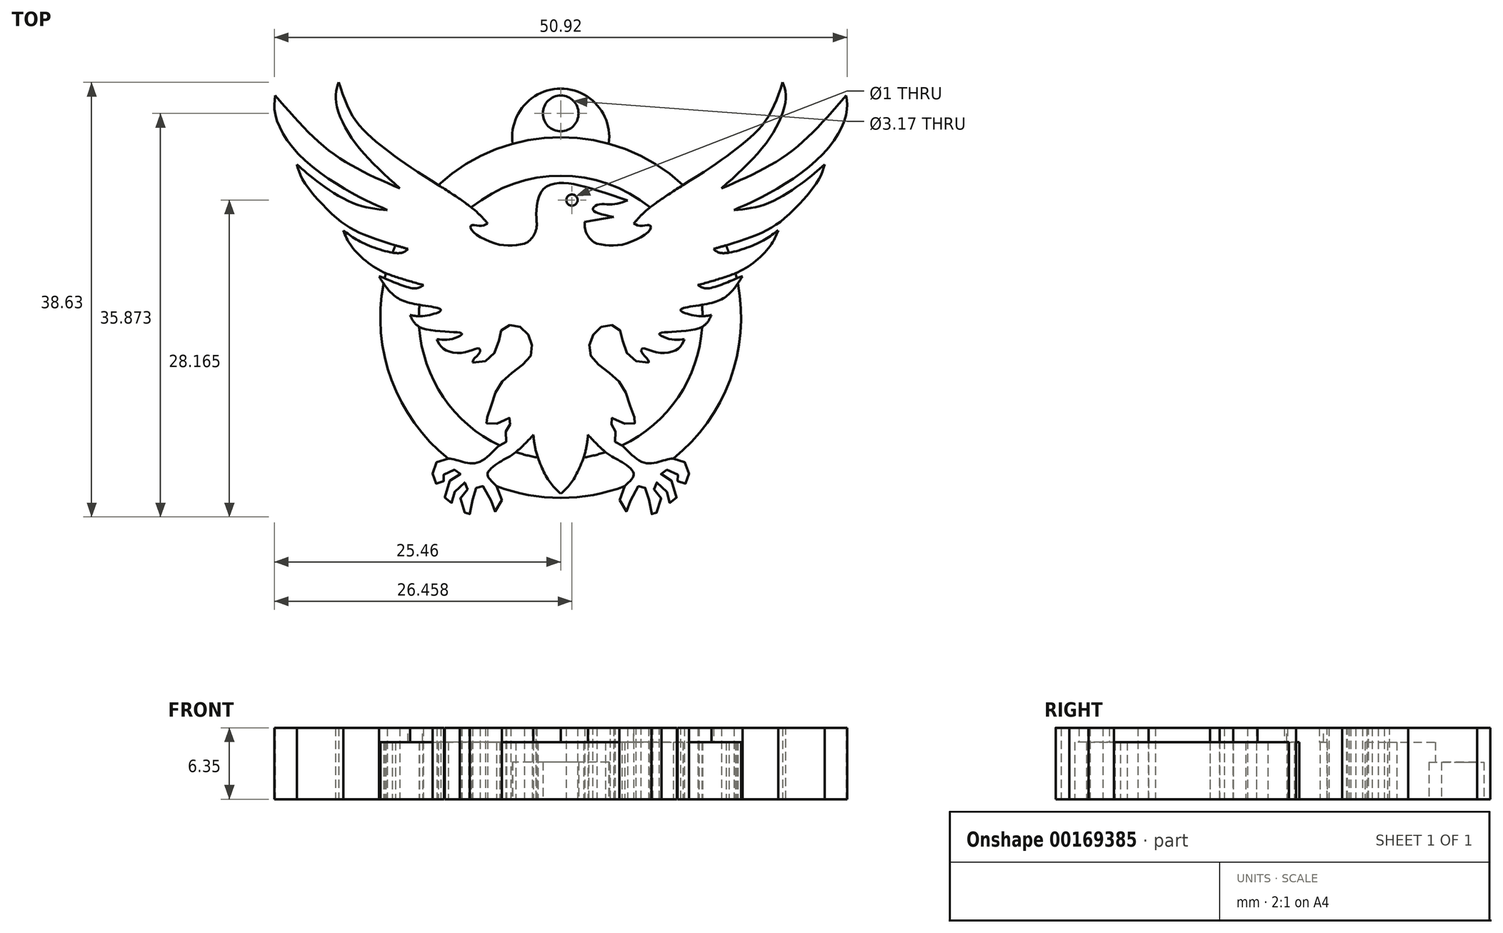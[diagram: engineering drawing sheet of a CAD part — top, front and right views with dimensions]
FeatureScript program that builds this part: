
annotation { "Feature Type Name" : "Feature", "Feature Type Description" : "" }
export const myFeature = defineFeature(function(context is Context, id is Id, definition is map)
    precondition{}
    {
        {
            var Q0;
            Q0=qCreatedBy(makeId("Top.planeOp"),FACE);
            var sketch = newSketch(context, id + "F0", { "sketchPlane" : qUnion([Q0])});
            skArc(sketch, "E0", {"start": v(-3.37, -10.71) * mm, "mid": v(-3.14, -11.87) * mm, "end": v(-2.29, -12.67) * mm});
            skFitSpline(sketch, "E1", {"points": [v(-2.29, -12.67) * mm, v(0.23, -12.67) * mm, v(2.47, -11.32) * mm, v(2.37, -11.01) * mm, v(1.64, -11.08) * mm, v(0.98, -10.87) * mm], "startDerivative": vector(8.17, -1.32) * mm, "endDerivative": vector(-4, 2.15) * mm});
            skFitSpline(sketch, "E2", {"points": [v(0.98, -10.87) * mm, v(2.44, -9.44) * mm, v(7.37, -6.17) * mm, v(10.62, -3.82) * mm, v(12.83, -1.57) * mm, v(14.23, 1.68) * mm], "startDerivative": vector(7.54, 8.8) * mm, "endDerivative": vector(5.9, 17.53) * mm});
            skFitSpline(sketch, "E3", {"points": [v(14.23, 1.68) * mm, v(14.5, 0.33) * mm, v(13.2, -3.1) * mm, v(8.8, -7.74) * mm], "startDerivative": vector(2.08, -5.75) * mm, "endDerivative": vector(-11.1, -10.06) * mm});
            skFitSpline(sketch, "E4", {"points": [v(8.8, -7.74) * mm, v(14.77, -4.61) * mm, v(19.87, 0.5) * mm], "startDerivative": vector(12.68, 5.47) * mm, "endDerivative": vector(9.48, 11) * mm});
            skFitSpline(sketch, "E5", {"points": [v(19.87, 0.5) * mm, v(19.87, -1.18) * mm, v(17.7, -4.8) * mm, v(12.52, -8.44) * mm, v(9.9, -9.66) * mm], "startDerivative": vector(1.23, -9.08) * mm, "endDerivative": vector(-10.45, -4.42) * mm});
            skFitSpline(sketch, "E6", {"points": [v(9.9, -9.66) * mm, v(12.85, -9.1) * mm, v(16.4, -6.93) * mm, v(17.95, -5.6) * mm], "startDerivative": vector(8.57, 0.68) * mm, "endDerivative": vector(4.89, 4.45) * mm});
            skFitSpline(sketch, "E7", {"points": [v(17.95, -5.6) * mm, v(17.36, -7.07) * mm, v(14.57, -10.25) * mm, v(12.16, -11.78) * mm, v(8.07, -13.13) * mm], "startDerivative": vector(-1.97, -7.45) * mm, "endDerivative": vector(-15.16, -4.48) * mm});
            skFitSpline(sketch, "E8", {"points": [v(8.07, -13.13) * mm, v(8.8, -13.5) * mm, v(11.88, -12.67) * mm, v(13.82, -11.49) * mm], "startDerivative": vector(2.56, -2.28) * mm, "endDerivative": vector(4.6, 3.34) * mm});
            skFitSpline(sketch, "E9", {"points": [v(13.82, -11.49) * mm, v(13.1, -12.89) * mm, v(11, -14.78) * mm, v(8.8, -15.73) * mm, v(6.7, -16.34) * mm], "startDerivative": vector(-2.57, -6.45) * mm, "endDerivative": vector(-8.46, -2.36) * mm});
            skFitSpline(sketch, "E10", {"points": [v(6.7, -16.34) * mm, v(7.58, -16.63) * mm, v(10.33, -15.66) * mm, v(10.64, -15.57) * mm], "startDerivative": vector(2.24, -1.67) * mm, "endDerivative": vector(1.2, 0.2) * mm});
            skFitSpline(sketch, "E11", {"points": [v(10.64, -15.57) * mm, v(9.7, -16.9) * mm, v(8.07, -17.88) * mm, v(5.25, -18.44) * mm, v(5.17, -18.62) * mm, v(6.7, -19.09) * mm, v(7.89, -19) * mm], "startDerivative": vector(-4.95, -7.81) * mm, "endDerivative": vector(6.73, 1.3) * mm});
            skFitSpline(sketch, "E12", {"points": [v(7.89, -19) * mm, v(6.86, -20.15) * mm, v(3.5, -20.57) * mm, v(3.27, -20.71) * mm, v(4.27, -21.16) * mm, v(5.5, -21.16) * mm], "startDerivative": vector(-2.87, -6.23) * mm, "endDerivative": vector(5.96, 0.75) * mm});
            skFitSpline(sketch, "E13", {"points": [v(5.5, -21.16) * mm, v(4.87, -22.04) * mm, v(3.02, -22.32) * mm, v(1.8, -21.98) * mm, v(1.66, -22.24) * mm, v(2.22, -22.94) * mm, v(2.32, -23.25) * mm], "startDerivative": vector(-2.34, -5.3) * mm, "endDerivative": vector(0.24, -2.7) * mm});
            skFitSpline(sketch, "E14", {"points": [v(2.32, -23.25) * mm, v(0.8, -22.88) * mm, v(0, -21.38) * mm, v(-0.27, -20.31) * mm, v(-1.2, -19.9) * mm, v(-2.29, -20.33) * mm, v(-2.9, -21.44) * mm, v(-2.86, -22.58) * mm, v(-1.78, -23.69) * mm, v(-0.41, -24.83) * mm, v(0.45, -26.34) * mm, v(0.98, -28) * mm, v(1.18, -28.53) * mm, v(0.45, -28.7) * mm, v(-0.45, -28.43) * mm, v(-0.77, -28.1) * mm, v(-1.01, -28.23) * mm, v(-1.01, -28.7) * mm, v(-0.65, -29.23) * mm, v(-0.67, -30.28) * mm, v(-0.21, -30.52) * mm, v(1.7, -32.07) * mm, v(3.59, -31.95) * mm, v(4.81, -31.78) * mm, v(5.72, -32.33) * mm, v(5.86, -33.43) * mm, v(5.5, -34.01) * mm, v(4.87, -33.83) * mm, v(5.15, -33.4) * mm, v(4.35, -33.01) * mm, v(3.75, -32.75) * mm, v(3.4, -33.11) * mm, v(4.25, -33.65) * mm, v(4.71, -35.5) * mm, v(4.2, -35.72) * mm, v(4.03, -34.98) * mm, v(3.06, -33.9) * mm, v(2.68, -34.28) * mm, v(3.04, -34.74) * mm, v(3.43, -35.82) * mm, v(2.6, -36.95) * mm, v(2.6, -36.24) * mm, v(2.04, -34.7) * mm, v(1.94, -34.2) * mm, v(1.38, -34.24) * mm, v(0.51, -36.1) * mm, v(0.31, -36.47) * mm, v(-0.3, -35.22) * mm, v(0.55, -33.85) * mm, v(0.98, -33.1) * mm, v(0, -32.13) * mm, v(-1.38, -31.3) * mm, v(-3.08, -29.65) * mm], "startDerivative": vector(-71.1, 3.05) * mm, "endDerivative": vector(-59.57, 64.05) * mm});
            skFitSpline(sketch, "E15", {"points": [v(-3.08, -29.65) * mm, v(-3.34, -31.24) * mm, v(-4.47, -33.75) * mm, v(-5.51, -34.9) * mm], "startDerivative": vector(-0.44, -4.8) * mm, "endDerivative": vector(-3.51, -3.2) * mm});
            skArc(sketch, "E16.MirrorCS", {"start": v(-7.65, -10.71) * mm, "mid": v(-7.88, -11.87) * mm, "end": v(-8.73, -12.67) * mm});
            skFitSpline(sketch, "E17.MirrorCS", {"points": [v(-8.73, -12.67) * mm, v(-11.25, -12.67) * mm, v(-13.5, -11.32) * mm, v(-13.4, -11.01) * mm, v(-12.66, -11.08) * mm, v(-12, -10.87) * mm], "startDerivative": vector(-8.17, -1.32) * mm, "endDerivative": vector(4, 2.15) * mm});
            skFitSpline(sketch, "E18.MirrorCS", {"points": [v(-12, -10.87) * mm, v(-13.46, -9.44) * mm, v(-18.4, -6.17) * mm, v(-21.64, -3.82) * mm, v(-23.85, -1.57) * mm, v(-25.25, 1.68) * mm], "startDerivative": vector(-7.54, 8.8) * mm, "endDerivative": vector(-5.9, 17.53) * mm});
            skFitSpline(sketch, "E19.MirrorCS", {"points": [v(-25.25, 1.68) * mm, v(-25.52, 0.33) * mm, v(-24.21, -3.1) * mm, v(-19.82, -7.74) * mm], "startDerivative": vector(-2.08, -5.75) * mm, "endDerivative": vector(11.1, -10.06) * mm});
            skFitSpline(sketch, "E20.MirrorCS", {"points": [v(-19.82, -7.74) * mm, v(-25.8, -4.61) * mm, v(-30.89, 0.5) * mm], "startDerivative": vector(-12.68, 5.47) * mm, "endDerivative": vector(-9.48, 11) * mm});
            skFitSpline(sketch, "E21.MirrorCS", {"points": [v(-30.89, 0.5) * mm, v(-30.89, -1.18) * mm, v(-28.72, -4.8) * mm, v(-23.54, -8.44) * mm, v(-20.92, -9.66) * mm], "startDerivative": vector(-1.23, -9.08) * mm, "endDerivative": vector(10.45, -4.42) * mm});
            skFitSpline(sketch, "E22.MirrorCS", {"points": [v(-20.92, -9.66) * mm, v(-23.87, -9.1) * mm, v(-27.42, -6.93) * mm, v(-28.97, -5.6) * mm], "startDerivative": vector(-8.57, 0.68) * mm, "endDerivative": vector(-4.89, 4.45) * mm});
            skFitSpline(sketch, "E23.MirrorCS", {"points": [v(-28.97, -5.6) * mm, v(-28.38, -7.07) * mm, v(-25.59, -10.25) * mm, v(-23.18, -11.78) * mm, v(-19.1, -13.13) * mm], "startDerivative": vector(1.97, -7.45) * mm, "endDerivative": vector(15.16, -4.48) * mm});
            skFitSpline(sketch, "E24.MirrorCS", {"points": [v(-19.1, -13.13) * mm, v(-19.82, -13.5) * mm, v(-22.9, -12.67) * mm, v(-24.84, -11.49) * mm], "startDerivative": vector(-2.56, -2.28) * mm, "endDerivative": vector(-4.6, 3.34) * mm});
            skFitSpline(sketch, "E25.MirrorCS", {"points": [v(-24.84, -11.49) * mm, v(-24.12, -12.89) * mm, v(-22.03, -14.78) * mm, v(-19.82, -15.73) * mm, v(-17.72, -16.34) * mm], "startDerivative": vector(2.57, -6.45) * mm, "endDerivative": vector(8.46, -2.36) * mm});
            skFitSpline(sketch, "E26.MirrorCS", {"points": [v(-17.72, -16.34) * mm, v(-18.6, -16.63) * mm, v(-21.35, -15.66) * mm, v(-21.66, -15.57) * mm], "startDerivative": vector(-2.24, -1.67) * mm, "endDerivative": vector(-1.2, 0.2) * mm});
            skFitSpline(sketch, "E27.MirrorCS", {"points": [v(-21.66, -15.57) * mm, v(-20.72, -16.9) * mm, v(-19.1, -17.88) * mm, v(-16.27, -18.44) * mm, v(-16.2, -18.62) * mm, v(-17.72, -19.09) * mm, v(-18.9, -19) * mm], "startDerivative": vector(4.95, -7.81) * mm, "endDerivative": vector(-6.73, 1.3) * mm});
            skFitSpline(sketch, "E28.MirrorCS", {"points": [v(-18.9, -19) * mm, v(-17.88, -20.15) * mm, v(-14.53, -20.57) * mm, v(-14.29, -20.71) * mm, v(-15.3, -21.16) * mm, v(-16.52, -21.16) * mm], "startDerivative": vector(2.87, -6.23) * mm, "endDerivative": vector(-5.96, 0.75) * mm});
            skFitSpline(sketch, "E29.MirrorCS", {"points": [v(-16.52, -21.16) * mm, v(-15.9, -22.04) * mm, v(-14.04, -22.32) * mm, v(-12.82, -21.98) * mm, v(-12.68, -22.24) * mm, v(-13.24, -22.94) * mm, v(-13.34, -23.25) * mm], "startDerivative": vector(2.34, -5.3) * mm, "endDerivative": vector(-0.24, -2.7) * mm});
            skFitSpline(sketch, "E30.MirrorCS", {"points": [v(-13.34, -23.25) * mm, v(-11.81, -22.88) * mm, v(-11.02, -21.38) * mm, v(-10.75, -20.31) * mm, v(-9.83, -19.9) * mm, v(-8.73, -20.33) * mm, v(-8.12, -21.44) * mm, v(-8.16, -22.58) * mm, v(-9.24, -23.69) * mm, v(-10.6, -24.83) * mm, v(-11.47, -26.34) * mm, v(-12, -28) * mm, v(-12.2, -28.53) * mm, v(-11.47, -28.7) * mm, v(-10.57, -28.43) * mm, v(-10.25, -28.1) * mm, v(-10, -28.23) * mm, v(-10, -28.7) * mm, v(-10.37, -29.23) * mm, v(-10.35, -30.28) * mm, v(-10.8, -30.52) * mm, v(-12.72, -32.07) * mm, v(-14.6, -31.95) * mm, v(-15.83, -31.78) * mm, v(-16.74, -32.33) * mm, v(-16.88, -33.43) * mm, v(-16.52, -34.01) * mm, v(-15.9, -33.83) * mm, v(-16.17, -33.4) * mm, v(-15.37, -33.01) * mm, v(-14.77, -32.75) * mm, v(-14.43, -33.11) * mm, v(-15.27, -33.65) * mm, v(-15.73, -35.5) * mm, v(-15.23, -35.72) * mm, v(-15.05, -34.98) * mm, v(-14.08, -33.9) * mm, v(-13.7, -34.28) * mm, v(-14.06, -34.74) * mm, v(-14.45, -35.82) * mm, v(-13.62, -36.95) * mm, v(-13.62, -36.24) * mm, v(-13.06, -34.7) * mm, v(-12.96, -34.2) * mm, v(-12.4, -34.24) * mm, v(-11.53, -36.1) * mm, v(-11.33, -36.47) * mm, v(-10.73, -35.22) * mm, v(-11.57, -33.85) * mm, v(-12, -33.1) * mm, v(-11.02, -32.13) * mm, v(-9.64, -31.3) * mm, v(-7.94, -29.65) * mm], "startDerivative": vector(71.1, 3.05) * mm, "endDerivative": vector(59.57, 64.05) * mm});
            skFitSpline(sketch, "E31.MirrorCS", {"points": [v(-7.94, -29.65) * mm, v(-7.68, -31.24) * mm, v(-6.55, -33.75) * mm, v(-5.51, -34.9) * mm], "startDerivative": vector(0.44, -4.8) * mm, "endDerivative": vector(3.51, -3.2) * mm});
            skArc(sketch, "E32", {"start": v(-11.21, -34.22) * mm, "mid": v(-5.51, -35.27) * mm, "end": v(0.2, -34.22) * mm});
            skArc(sketch, "E33", {"start": v(-9.5, -31.2) * mm, "mid": v(-8.53, -31.47) * mm, "end": v(-7.54, -31.68) * mm});
            skFitSpline(sketch, "E34", {"points": [v(-7.65, -10.71) * mm, v(-7.65, -9.41) * mm, v(-7.12, -7.88) * mm, v(-5.8, -7.27) * mm, v(-3.69, -7.51) * mm, v(0.44, -8.8) * mm], "startDerivative": vector(-0.46, 7.77) * mm, "endDerivative": vector(15.27, -5.17) * mm});
            skFitSpline(sketch, "E35", {"points": [v(0.44, -8.8) * mm, v(-0.98, -9.16) * mm, v(-2.24, -9.2) * mm, v(-2.65, -9.64) * mm, v(-0.81, -10.28) * mm], "startDerivative": vector(-5.23, -1.83) * mm, "endDerivative": vector(8.52, -1.74) * mm});
            skLineSegment(sketch, "E36", {"start": v(-3.37, -10.71) * mm, "end": v(-0.81, -10.28) * mm});
            skCircle(sketch, "E37", {"center": v(-4.51, -8.78) * mm, "radius": 0.5 * mm});
            skArc(sketch, "E38", {"start": v(-1.23, -3.77) * mm, "mid": v(-5.51, 1.12) * mm, "end": v(-9.79, -3.77) * mm});
            skCircle(sketch, "E39", {"center": v(-5.51, -1.08) * mm, "radius": 1.59 * mm});
            skArc(sketch, "E40.trimOffspring", {"start": v(-0.07, -30.6) * mm, "mid": v(4.93, -26.3) * mm, "end": v(7.07, -20.05) * mm});
            skArc(sketch, "E41.trimOffspring", {"start": v(-3.48, -31.68) * mm, "mid": v(-2.49, -31.47) * mm, "end": v(-1.52, -31.2) * mm});
            skArc(sketch, "E42.trimOffspring", {"start": v(4.49, -31.77) * mm, "mid": v(9.53, -24.78) * mm, "end": v(10.24, -16.2) * mm});
            skArc(sketch, "E43.trimOffspring", {"start": v(6.78, -16.4) * mm, "mid": v(6.77, -16.36) * mm, "end": v(6.76, -16.32) * mm});
            skArc(sketch, "E44.trimOffspring", {"start": v(7.1, -19.1) * mm, "mid": v(7.09, -18.6) * mm, "end": v(7.05, -18.1) * mm});
            skArc(sketch, "E45.trimOffspring", {"start": v(9.45, -13.46) * mm, "mid": v(9.32, -13.13) * mm, "end": v(9.18, -12.8) * mm});
            skArc(sketch, "E46.trimOffspring", {"start": v(5.37, -7.45) * mm, "mid": v(-5.51, -3.2) * mm, "end": v(-16.39, -7.45) * mm});
            skArc(sketch, "E47.trimOffspring", {"start": v(2.44, -9.44) * mm, "mid": v(-5.51, -6.62) * mm, "end": v(-13.46, -9.44) * mm});
            skArc(sketch, "E48.trimOffspring", {"start": v(-17.78, -16.32) * mm, "mid": v(-17.79, -16.36) * mm, "end": v(-17.8, -16.4) * mm});
            skArc(sketch, "E49.trimOffspring", {"start": v(-18.07, -18.1) * mm, "mid": v(-18.1, -18.6) * mm, "end": v(-18.12, -19.1) * mm});
            skArc(sketch, "E50.trimOffspring", {"start": v(-18.1, -20.05) * mm, "mid": v(-15.95, -26.3) * mm, "end": v(-10.95, -30.6) * mm});
            skArc(sketch, "E51.trimOffspring", {"start": v(-20.2, -12.8) * mm, "mid": v(-20.34, -13.13) * mm, "end": v(-20.47, -13.46) * mm});
            skArc(sketch, "E52.trimOffspring", {"start": v(-21.05, -15.28) * mm, "mid": v(-21.1, -15.5) * mm, "end": v(-21.16, -15.74) * mm});
            skArc(sketch, "E53.trimOffspring", {"start": v(-21.26, -16.2) * mm, "mid": v(-20.55, -24.78) * mm, "end": v(-15.5, -31.77) * mm});
            skArc(sketch, "E54.trimOffspring", {"start": v(10.14, -15.74) * mm, "mid": v(10.09, -15.5) * mm, "end": v(10.03, -15.28) * mm});
            skSolve(sketch);
        }
        {
            var Q0;
            Q0=makeQuery(id+"F0.imprint","IMPRINT",FACE,{"disambiguationData":[TD([[makeQuery(id+"F0.imprint","IMPRINT",EDGE,{"derivedFrom":sQuery(id+"F0.wireOp",EDGE,"E0")}),-1.0]])]});
            extrude(context, id + "F1", {"entities" : qUnion([Q0]), "depth" : 6.35 * mm});
        }
        {
            var Q0;
            {var subQ8=sQuery(id+"F0.wireOp",EDGE,"E47.trimOffspring");Q0=makeQuery(id+"F0.imprint","IMPRINT",FACE,{"disambiguationData":[TD([[makeQuery(id+"F0.imprint","IMPRINT",EDGE,{"derivedFrom":subQ8}),-1.0]])]});}
            var Q1;
            {var subQ3=sQuery(id+"F0.wireOp",EDGE,"E49.trimOffspring");Q1=makeQuery(id+"F0.imprint","IMPRINT",FACE,{"disambiguationData":[TD([[makeQuery(id+"F0.imprint","IMPRINT",EDGE,{"derivedFrom":subQ3}),-1.0]])]});}
            var Q2;
            {var subQ0=sQuery(id+"F0.wireOp",EDGE,"E48.trimOffspring");Q2=makeQuery(id+"F0.imprint","IMPRINT",FACE,{"disambiguationData":[TD([[makeQuery(id+"F0.imprint","IMPRINT",EDGE,{"derivedFrom":subQ0}),-1.0]])]});}
            var Q3;
            {var subQ3=sQuery(id+"F0.wireOp",EDGE,"E51.trimOffspring");Q3=makeQuery(id+"F0.imprint","IMPRINT",FACE,{"disambiguationData":[TD([[makeQuery(id+"F0.imprint","IMPRINT",EDGE,{"derivedFrom":subQ3}),1.0]])]});}
            var Q4;
            {var subQ3=sQuery(id+"F0.wireOp",EDGE,"E45.trimOffspring");Q4=makeQuery(id+"F0.imprint","IMPRINT",FACE,{"disambiguationData":[TD([[makeQuery(id+"F0.imprint","IMPRINT",EDGE,{"derivedFrom":subQ3}),1.0]])]});}
            var Q5;
            {var subQ0=sQuery(id+"F0.wireOp",EDGE,"E43.trimOffspring");Q5=makeQuery(id+"F0.imprint","IMPRINT",FACE,{"disambiguationData":[TD([[makeQuery(id+"F0.imprint","IMPRINT",EDGE,{"derivedFrom":subQ0}),-1.0]])]});}
            var Q6;
            {var subQ0=sQuery(id+"F0.wireOp",EDGE,"E40.trimOffspring");Q6=makeQuery(id+"F0.imprint","IMPRINT",FACE,{"disambiguationData":[TD([[makeQuery(id+"F0.imprint","IMPRINT",EDGE,{"derivedFrom":subQ0}),-1.0]])]});}
            var Q7;
            {var subQ4=sQuery(id+"F0.wireOp",EDGE,"E32");Q7=makeQuery(id+"F0.imprint","IMPRINT",FACE,{"disambiguationData":[TD([[makeQuery(id+"F0.imprint","IMPRINT",EDGE,{"derivedFrom":subQ4}),1.0]])]});}
            extrude(context, id + "F2", {"entities" : qUnion([Q0, Q1, Q2, Q3, Q4, Q5, Q6, Q7]), "operationType" : NewBodyOperationType.ADD, "depth" : 5.08 * mm});
        }
        {
            var Q0;
            {var subQ0=sQuery(id+"F0.wireOp",EDGE,"E38");Q0=makeQuery(id+"F0.imprint","IMPRINT",FACE,{"disambiguationData":[TD([[makeQuery(id+"F0.imprint","IMPRINT",EDGE,{"derivedFrom":subQ0}),1.0]])]});}
            extrude(context, id + "F3", {"entities" : qUnion([Q0]), "operationType" : NewBodyOperationType.ADD, "depth" : 3.3 * mm});
        }
    });
